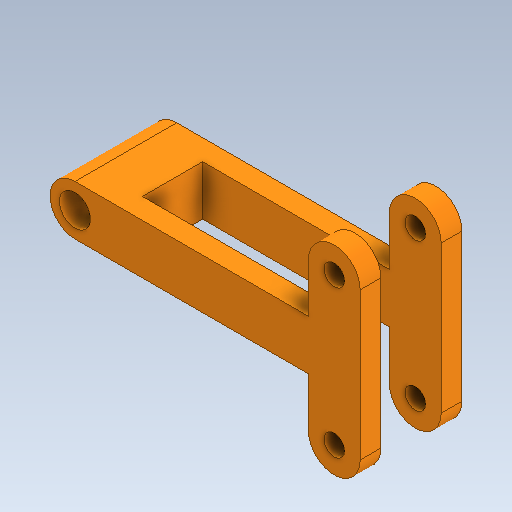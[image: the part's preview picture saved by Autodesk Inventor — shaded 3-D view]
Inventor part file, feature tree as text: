
AUTODESK INVENTOR PART (.ipt)
format: ipt  version: 2020 (Build 240168000, 168)  size: 194,560 bytes
history: native  units: in
note: dims shown in document units (in); Inventor stores cm internally (conversion verified against a paired STEP export)
features: extrude x3, sketch x3, projected_geometry x2, mirror x1
ambient origin geometry x8: Origin, YZ Plane, XZ Plane, XY Plane, X Axis, Y Axis, Z Axis, Center Point
bodies: Solid1 (feature_tree)
feature tree (9):
  extrude  "Extrusion1"  Depth=0.2797in
  extrude  "Extrusion2"  Depth=0.1969in
  extrude  "Extrusion4"  Depth=0.0787in
  mirror  "Mirror2"
  sketch  "Sketch1"  dims[d0=0.2797in d1=0.2797in]
  sketch  "Sketch2"  dims[d2=0.1969in d3=0.1969in]
  projected_geometry  "Projected Loop1"
  sketch  "Sketch4"  dims[d4=0.1969in d5=0.0787in d6=0.0787in d7=0.0945in d8=0.8071in d9=0.189in d10=0.0787in d11=0.0in d12=0.1144in d13=0.0in d21=0.0787in d22=0.1181in d23=0.189in d24=0.3937in d25=0.0in d26=0.0984in d18=0.0197in d19=0.0344in d20=0.0197in]
  projected_geometry  "Projected Loop3"
